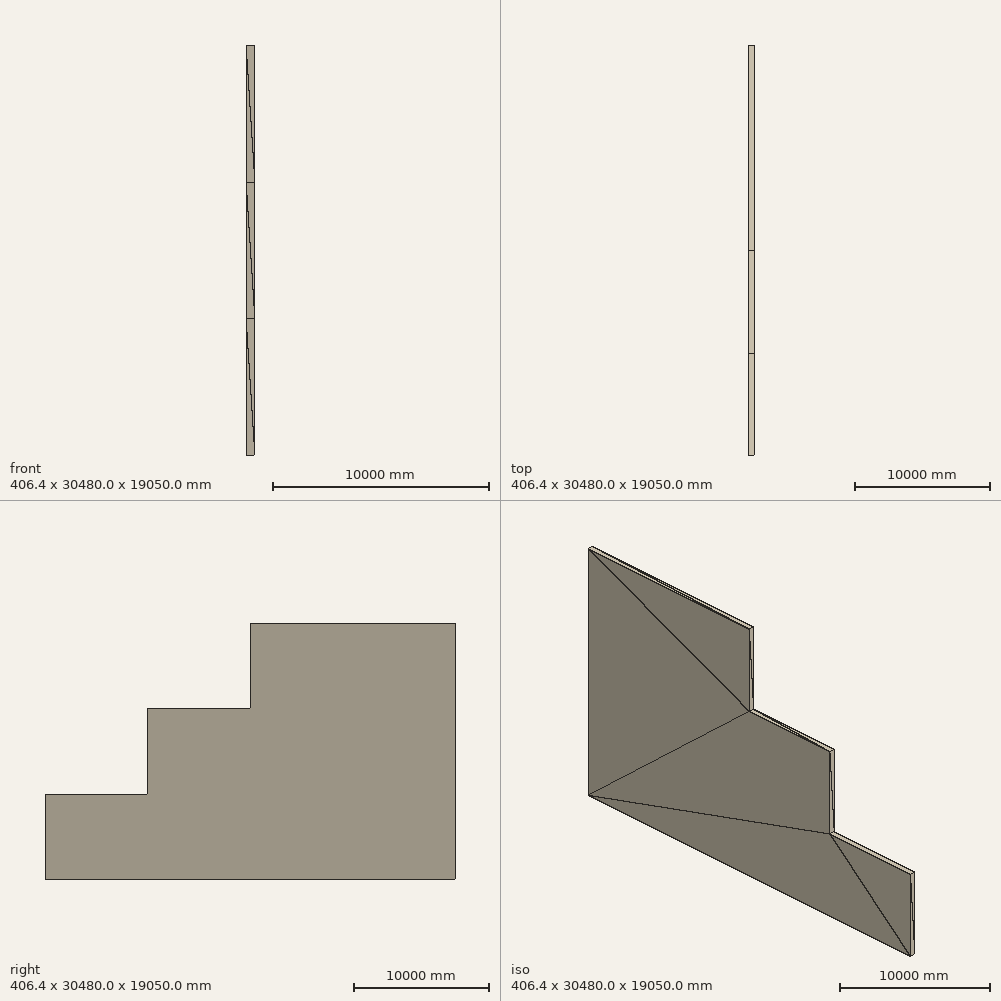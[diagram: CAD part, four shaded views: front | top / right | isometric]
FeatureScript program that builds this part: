
annotation { "Feature Type Name" : "Feature", "Feature Type Description" : "" }
export const myFeature = defineFeature(function(context is Context, id is Id, definition is map)
    precondition{}
    {
        {
            var Q0;
            Q0=qCreatedBy(makeId("Right.planeOp"),FACE);
            var sketch = newSketch(context, id + "F0", { "sketchPlane" : qUnion([Q0])});
            skLineSegment(sketch, "E0", {"start": v(0, 0) * mm, "end": v(-30480, 0) * mm});
            skLineSegment(sketch, "E1", {"start": v(-30480, 0) * mm, "end": v(-30480, 6350) * mm});
            skLineSegment(sketch, "E2", {"start": v(-30480, 6350) * mm, "end": v(-22860, 6350) * mm});
            skLineSegment(sketch, "E3", {"start": v(-22860, 6350) * mm, "end": v(-22860, 12700) * mm});
            skLineSegment(sketch, "E4", {"start": v(-22860, 12700) * mm, "end": v(-15240, 12700) * mm});
            skLineSegment(sketch, "E5", {"start": v(-15240, 12700) * mm, "end": v(-15240, 19050) * mm});
            skLineSegment(sketch, "E6", {"start": v(-15240, 19050) * mm, "end": v(0, 19050) * mm});
            skLineSegment(sketch, "E7", {"start": v(0, 19050) * mm, "end": v(0, 0) * mm});
            skSolve(sketch);
        }
        {
            var Q0;
            Q0 = qSketchRegion(id + "F0", true);
            extrude(context, id + "F1", {"entities" : qUnion([Q0]), "depth" : 406.4 * mm, "offsetDistance" : 25.4 * mm});
        }
    });
